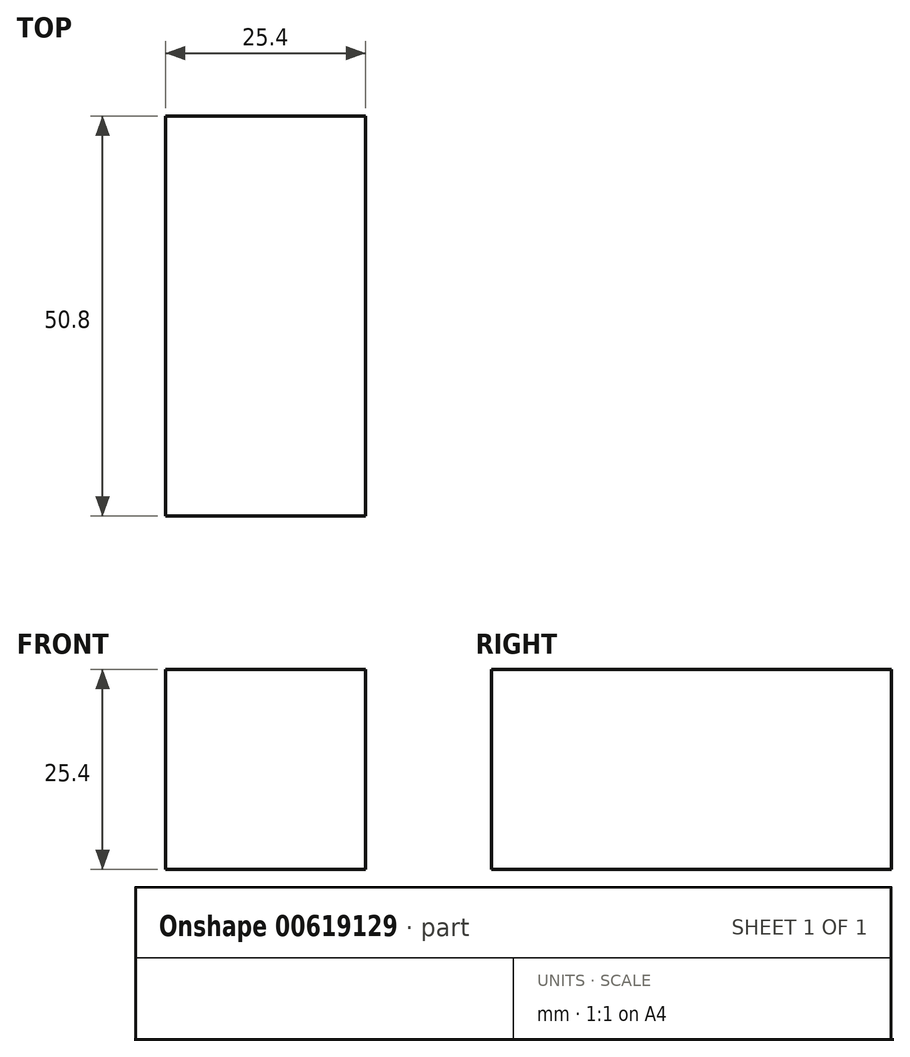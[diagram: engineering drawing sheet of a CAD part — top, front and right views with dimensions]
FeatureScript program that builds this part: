
annotation { "Feature Type Name" : "Feature", "Feature Type Description" : "" }
export const myFeature = defineFeature(function(context is Context, id is Id, definition is map)
    precondition{}
    {
        {
            var Q0;
            Q0=qCreatedBy(makeId("Front.planeOp"),FACE);
            var sketch = newSketch(context, id + "F0", { "sketchPlane" : qUnion([Q0])});
            skLineSegment(sketch, "E0.bottom", {"start": v(-12.7, 12.7) * mm, "end": v(12.7, 12.7) * mm});
            skLineSegment(sketch, "E0.top", {"start": v(-12.7, -12.7) * mm, "end": v(12.7, -12.7) * mm});
            skLineSegment(sketch, "E0.left", {"start": v(-12.7, 12.7) * mm, "end": v(-12.7, -12.7) * mm});
            skLineSegment(sketch, "E0.right", {"start": v(12.7, 12.7) * mm, "end": v(12.7, -12.7) * mm});
            skPoint(sketch, "E0.middle", {"position": v(0, 0) * mm});
            skSolve(sketch);
        }
        {
            var Q0;
            Q0 = qSketchRegion(id + "F0", true);
            extrude(context, id + "F1", {"entities" : qUnion([Q0]), "depth" : 50.8 * mm, "offsetDistance" : 25.4 * mm});
        }
    });
